# Revit family: Domotics-DomesticRanges-GEWISS-SYSTEM_POWER-SOCKET-OUTLET_SELV
name_source: partatom
category: Apparecchi elettrici
revit_build: Autodesk Revit 2016 (Build: 20161004_0715(x64)
units: mm (PartAtom-declared; Revit-internal decimal feet)

## family parameters
Condiviso = Sì
Host = Superficie
Mantenere orientamento annotazione = Sì
Punto di calcolo locali = Sì
Quota connettore circolare = Usa diametro
Taglio con vuoti quando caricato = Sì
Tipo di parte = Normale

## types (2) — shared parameters
Carico apparente = 0 VA
Catalogue = DOMOTICS
Catalogue Range = SYSTEM - DOMESTIC RANGE
Centre distance = 12,4MM
Description: = 2P - 6A - 24V
Electrocod = 0131
For plug pins = Ã˜ 3 mm
IDF = b1934aa8-3b83-4d95-84d8-9b7d365c25ca
IDT = 284d53f3-d621-47bc-a15e-241f232f9a30
Immagine tipo = GW21239.jpg
N. poli = 1
No. SYSTEM modules = 1
Produttore = GEWISS S.p.A.
Prospetto di default = 1219 mm
SEO = Socket outlet
Technical sheet = https://www.gewiss.com
Tipo_ = SYSTEM PRESE SELV_GENERICO : GW21239 Presa 2P 6A 24V (SELV) nero
URL = https://www.gewiss.com
Version file RFA = 19.4
Volt = 230 V

## per-type parameters (varying)
| type | Colour | Descrizione | EAN code | Modello |
| GW20239 - 2P 6A 24V SPECIAL SOCKET OUTLET SY/WT | White | 2P 6A 24V SPECIAL SOCKET OUTLET SY/WT | 8011564000711 | GW20239 |
| GW21239 - 2P 6A 24V SPECIAL SOCKET OUTLET SY/BK | Black | 2P 6A 24V SPECIAL SOCKET OUTLET SY/BK | 8011564128767 | GW21239 |

## geometry (parser evidence)
native form markers: Sweep x2
no freeform markers — native parametric forms only
